# Revit family: IS_Connect2_K9264_BIM_FR
name_source: partatom
category: Plumbing Fixtures
revit_build: Autodesk Revit 2017 (Build: 20160225_1515(x64)
units: mm (PartAtom-declared; Revit-internal decimal feet)

## family parameters
Always vertical = No
Cut with Voids When Loaded = No
OmniClass Number = 23.45.05.14.21.11
OmniClass Title = Bath/Shower Units
Part Type = Normal
Room Calculation Point = No
Round Connector Dimension = Use Diameter
Shared = No
Work Plane-Based = No

## types (1)
- K9264EO - EU 1200 CORNER ENTRY (AS INSTALLED ON THE LEFT)
    Accessories = www.idealspec.fr
    Auteur = Ideal Standard
    Bim-NomDuProjet = ISI_IdealStandard_ShowersEnclosures_Connect2_K9264EO
    CodeBarre = 8014140456032
    Conformité = NF
    ConseilsDInstallation = https://www.idealstandard.fr
    Couleur = Verre Propre
    CoûtDeRemplacement = 0
    DateDeCréation = 17/10/2019
    DiamètreÉvacuation = 0
    Dimensions = 1200 x 1950 x 0mm
    DuréeDeVie = 2
    DuréeGarantie = 2
    DétailGarantie = Garantie du Fabricant
    EffectuéPar = 17/10/2019
    Espace = Interne
    Finition = Verre Trempe
    Forme = Rectangularie
    Hauteur = 1950 mm  [stored 6.39764 ft]
    IfcExportAs = IfcFurnitureType
    IfcExportType = USERDEFINED
    InformationsProduit = https://www.idealstandard.fr
    Installation instructions = https://www.idealstandard.com
    Largeur = 1200 mm
    LienUtile = https://www.idealstandard.fr
    Longueur = 0 mm  [stored 0 ft]
    Manufacturer = Ideal Standard
    Marque = Ideal Standard
    Matériel = Verre Trempé
    Model = K9264EO
    Nom = ShowersEnclosures_Connect2_K9264EO_IdealStandard
    PiècesDétachées = https://www.idealstandard.fr
    PoidsNet = 40
    PoignéesDePréhension = No
    PressionDeFonctionnement = 0
    Product group = Shower Enclosure
    Profondeur = 0 mm  [stored 0 ft]
    Receveur = No
    TestDePression = 0
    URL = https://www.idealstandard.fr
    Uniclass 2015 Code = Pr_40_20_06_79
    Uniclass 2015 Name = Shower enclosures
    Uniclass2015Version = v1.15
    UnitéDeMesure = Millimètres
    UnitéDeTemps = Ans
    UnitéMonétaire = €
    UrlDuFabricant = https://www.idealstandard.fr
    Version = 1

note: [stored X ft] marks values corroborated as IEEE doubles in the binary element streams (Revit-internal decimal feet)

## geometry (parser evidence)
native form markers: Sweep x2
no freeform markers — native parametric forms only
